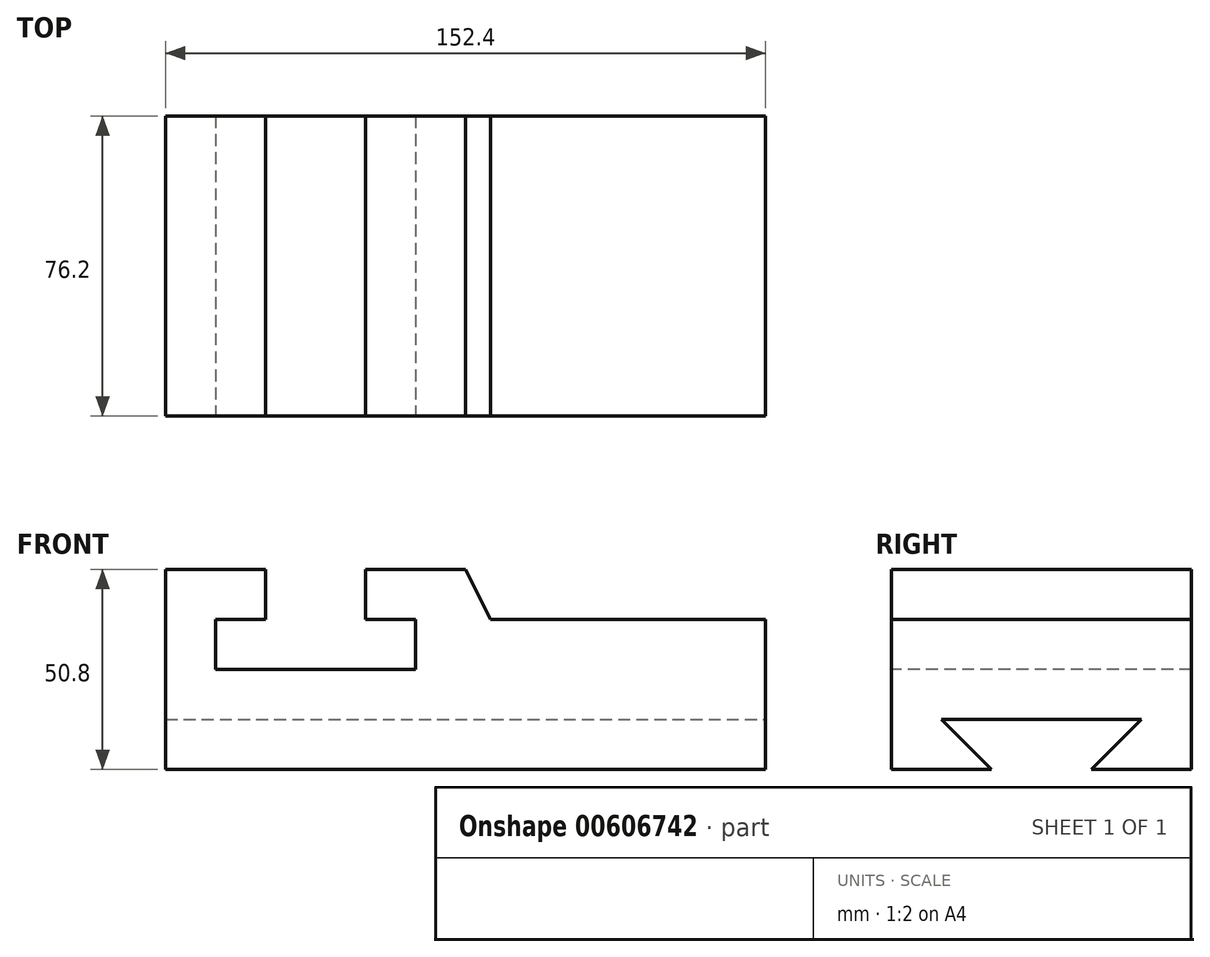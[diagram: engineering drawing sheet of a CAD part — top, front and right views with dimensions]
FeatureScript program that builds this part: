
annotation { "Feature Type Name" : "Feature", "Feature Type Description" : "" }
export const myFeature = defineFeature(function(context is Context, id is Id, definition is map)
    precondition{}
    {
        {
            var Q0;
            Q0=qCreatedBy(makeId("Front.planeOp"),FACE);
            var sketch = newSketch(context, id + "F0", { "sketchPlane" : qUnion([Q0])});
            skLineSegment(sketch, "E0.bottom", {"start": v(0, 0) * mm, "end": v(152.4, 0) * mm});
            skLineSegment(sketch, "E0.top", {"start": v(0, 50.8) * mm, "end": v(152.4, 50.8) * mm});
            skLineSegment(sketch, "E0.left", {"start": v(0, 0) * mm, "end": v(0, 50.8) * mm});
            skLineSegment(sketch, "E0.right", {"start": v(152.4, 0) * mm, "end": v(152.4, 50.8) * mm});
            skSolve(sketch);
        }
        {
            var Q0;
            Q0=makeQuery(id+"F0.imprint","IMPRINT",FACE,{"disambiguationData":[TD([[makeQuery(id+"F0.imprint","IMPRINT",EDGE,{"derivedFrom":sQuery(id+"F0.wireOp",EDGE,"E0.bottom")}),1.0]])]});
            extrude(context, id + "F1", {"entities" : qUnion([Q0]), "oppositeDirection" : true, "depth" : 76.2 * mm, "offsetDistance" : 25.4 * mm});
        }
        {
            var Q0;
            Q0=makeQuery(id+"F1.opExtrude","SWEPT_FACE",FACE,{"disambiguationData":[OSD([sQuery(id+"F0.wireOp",EDGE,"E0.right")])]});
            var sketch = newSketch(context, id + "F2", { "sketchPlane" : qUnion([Q0])});
            skLineSegment(sketch, "E1", {"start": v(25.4, 0) * mm, "end": v(12.7, 12.7) * mm});
            skLineSegment(sketch, "E2", {"start": v(12.7, 12.7) * mm, "end": v(63.5, 12.7) * mm});
            skLineSegment(sketch, "E3", {"start": v(63.5, 12.7) * mm, "end": v(50.8, 0) * mm});
            skLineSegment(sketch, "E4", {"start": v(25.4, 0) * mm, "end": v(50.8, 0) * mm});
            skSolve(sketch);
        }
        {
            var Q0;
            Q0 = qSketchRegion(id + "F2", true);
            extrude(context, id + "F3", {"entities" : qUnion([Q0]), "operationType" : NewBodyOperationType.REMOVE, "oppositeDirection" : true, "depth" : 152.4 * mm, "offsetDistance" : 25.4 * mm});
        }
        {
            var Q0;
            Q0=makeQuery(id+"F1.opExtrude","SWEPT_FACE",FACE,{"disambiguationData":[OSD([sQuery(id+"F0.wireOp",EDGE,"E0.top")])]});
            var sketch = newSketch(context, id + "F4", { "sketchPlane" : qUnion([Q0])});
            skLineSegment(sketch, "E5", {"start": v(0, 0) * mm, "end": v(82.55, 0) * mm});
            skLineSegment(sketch, "E6", {"start": v(82.55, 0) * mm, "end": v(82.55, 76.2) * mm});
            skSolve(sketch);
        }
        {
            var Q0;
            {var subQ0=sQuery(id+"F4.wireOp",EDGE,"E6");Q0=makeQuery(id+"F4.imprint","IMPRINT",FACE,{"disambiguationData":[TD([[makeQuery(id+"F4.imprint","IMPRINT",EDGE,{"derivedFrom":subQ0}),-1.0]])]});}
            extrude(context, id + "F5", {"entities" : qUnion([Q0]), "operationType" : NewBodyOperationType.REMOVE, "oppositeDirection" : true, "depth" : 12.7 * mm, "offsetDistance" : 25.4 * mm});
        }
        {
            var Q0;
            Q0=makeQuery(id+"F1.opExtrude","CAP_FACE",FACE,{"disambiguationData":[OSD([sQuery(id+"F0.wireOp",EDGE,"E0.bottom"),sQuery(id+"F0.wireOp",EDGE,"E0.top"),sQuery(id+"F0.wireOp",EDGE,"E0.left"),sQuery(id+"F0.wireOp",EDGE,"E0.right")])],"isStart":true});
            var sketch = newSketch(context, id + "F6", { "sketchPlane" : qUnion([Q0])});
            skLineSegment(sketch, "E7", {"start": v(76.2, 50.8) * mm, "end": v(82.55, 38.1) * mm});
            skLineSegment(sketch, "E8", {"start": v(82.55, 38.1) * mm, "end": v(82.55, 50.8) * mm});
            skLineSegment(sketch, "E9", {"start": v(82.55, 50.8) * mm, "end": v(76.2, 50.8) * mm});
            skSolve(sketch);
        }
        {
            var Q0;
            Q0 = qSketchRegion(id + "F6", true);
            extrude(context, id + "F7", {"entities" : qUnion([Q0]), "operationType" : NewBodyOperationType.REMOVE, "oppositeDirection" : true, "depth" : 143.26 * mm, "offsetDistance" : 25.4 * mm});
        }
        {
            var Q0;
            Q0=makeQuery(id+"F1.opExtrude","CAP_FACE",FACE,{"disambiguationData":[OSD([sQuery(id+"F0.wireOp",EDGE,"E0.bottom"),sQuery(id+"F0.wireOp",EDGE,"E0.top"),sQuery(id+"F0.wireOp",EDGE,"E0.left"),sQuery(id+"F0.wireOp",EDGE,"E0.right")])],"isStart":true});
            var sketch = newSketch(context, id + "F8", { "sketchPlane" : qUnion([Q0])});
            skLineSegment(sketch, "E10", {"start": v(0, 50.8) * mm, "end": v(0, 25.4) * mm});
            skLineSegment(sketch, "E11", {"start": v(0, 50.8) * mm, "end": v(25.4, 50.8) * mm});
            skLineSegment(sketch, "E12", {"start": v(25.4, 50.8) * mm, "end": v(25.4, 38.1) * mm});
            skLineSegment(sketch, "E13", {"start": v(25.4, 38.1) * mm, "end": v(12.7, 38.1) * mm});
            skLineSegment(sketch, "E14", {"start": v(12.7, 38.1) * mm, "end": v(12.7, 25.4) * mm});
            skLineSegment(sketch, "E15", {"start": v(12.7, 25.4) * mm, "end": v(63.5, 25.4) * mm});
            skLineSegment(sketch, "E16", {"start": v(63.5, 25.4) * mm, "end": v(63.5, 38.1) * mm});
            skLineSegment(sketch, "E17", {"start": v(63.5, 38.1) * mm, "end": v(50.8, 38.1) * mm});
            skLineSegment(sketch, "E18", {"start": v(50.8, 38.1) * mm, "end": v(50.8, 50.8) * mm});
            skSolve(sketch);
        }
        {
            var Q0;
            Q0 = qSketchRegion(id + "F8", true);
            var Q1;
            {var subQ0=sQuery(id+"F8.wireOp",EDGE,"E12");Q1=makeQuery(id+"F8.imprint","IMPRINT",FACE,{"disambiguationData":[TD([[makeQuery(id+"F8.imprint","IMPRINT",EDGE,{"derivedFrom":subQ0}),1.0]])]});}
            extrude(context, id + "F9", {"entities" : qUnion([Q0, Q1]), "operationType" : NewBodyOperationType.REMOVE, "oppositeDirection" : true, "depth" : 114.3 * mm, "offsetDistance" : 25.4 * mm});
        }
    });
